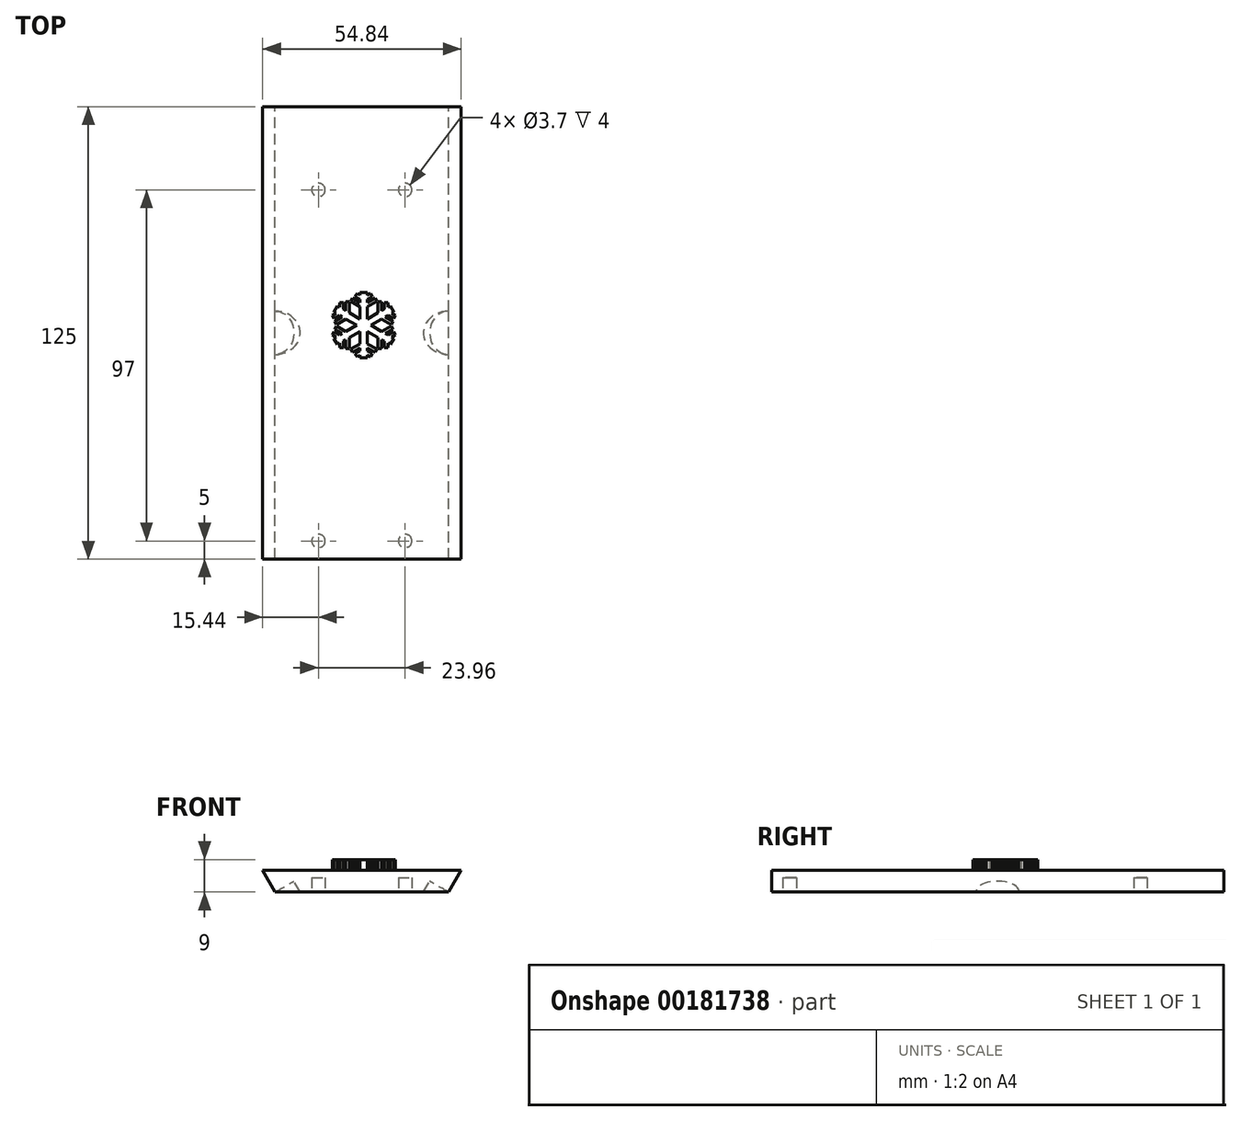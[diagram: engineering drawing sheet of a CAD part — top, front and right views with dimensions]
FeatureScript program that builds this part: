
annotation { "Feature Type Name" : "Feature", "Feature Type Description" : "" }
export const myFeature = defineFeature(function(context is Context, id is Id, definition is map)
    precondition{}
    {
        {
            var Q0;
            Q0=qCreatedBy(makeId("Front.planeOp"),FACE);
            var sketch = newSketch(context, id + "F0", { "sketchPlane" : qUnion([Q0])});
            skCircle(sketch, "E0.cCircle", {"center": v(0, 0) * mm, "radius": 47.5 * mm, "construction": true});
            skLineSegment(sketch, "E0.0", {"start": v(-27.42, -47.5) * mm, "end": v(-54.85, 0) * mm});
            skLineSegment(sketch, "E0.1", {"start": v(-54.85, 0) * mm, "end": v(-27.42, 47.5) * mm});
            skLineSegment(sketch, "E0.2", {"start": v(-27.42, 47.5) * mm, "end": v(27.42, 47.5) * mm});
            skLineSegment(sketch, "E0.3", {"start": v(27.42, 47.5) * mm, "end": v(54.85, 0) * mm});
            skLineSegment(sketch, "E0.4", {"start": v(54.85, 0) * mm, "end": v(27.42, -47.5) * mm});
            skLineSegment(sketch, "E0.5", {"start": v(27.42, -47.5) * mm, "end": v(-27.42, -47.5) * mm});
            skPoint(sketch, "E0.0.midPoint", {"position": v(-41.14, -23.75) * mm});
            skCircle(sketch, "E1.cCircle", {"center": v(0, 0) * mm, "radius": 41.5 * mm, "construction": true});
            skLineSegment(sketch, "E1.0", {"start": v(-23.96, -41.5) * mm, "end": v(-47.92, 0) * mm});
            skLineSegment(sketch, "E1.1", {"start": v(-47.92, 0) * mm, "end": v(-23.96, 41.5) * mm});
            skLineSegment(sketch, "E1.2", {"start": v(-23.96, 41.5) * mm, "end": v(23.96, 41.5) * mm});
            skLineSegment(sketch, "E1.3", {"start": v(23.96, 41.5) * mm, "end": v(47.92, 0) * mm});
            skLineSegment(sketch, "E1.4", {"start": v(47.92, 0) * mm, "end": v(23.96, -41.5) * mm});
            skLineSegment(sketch, "E1.5", {"start": v(23.96, -41.5) * mm, "end": v(-23.96, -41.5) * mm});
            skPoint(sketch, "E1.0.midPoint", {"position": v(-35.94, -20.75) * mm});
            skLineSegment(sketch, "E2", {"start": v(27.42, 47.5) * mm, "end": v(23.96, 41.5) * mm});
            skLineSegment(sketch, "E3", {"start": v(-27.42, 47.5) * mm, "end": v(-23.96, 41.5) * mm});
            skSolve(sketch);
        }
        {
            var Q0;
            Q0=makeQuery(id+"F0.imprint","IMPRINT",FACE,{"disambiguationData":[TD([[makeQuery(id+"F0.imprint","IMPRINT",EDGE,{"derivedFrom":sQuery(id+"F0.wireOp",EDGE,"E0.2")}),-1.0]])]});
            extrude(context, id + "F1", {"entities" : qUnion([Q0]), "depth" : 125 * mm});
        }
        {
            var Q0;
            Q0=makeQuery(id+"F1.opExtrude","SWEPT_FACE",FACE,{"disambiguationData":[OSD([sQuery(id+"F0.wireOp",EDGE,"E1.2")])]});
            var sketch = newSketch(context, id + "F2", { "sketchPlane" : qUnion([Q0])});
            skPoint(sketch, "E4", {"position": v(0, 125) * mm});
            skPoint(sketch, "E5", {"position": v(0, 120) * mm});
            skLineSegment(sketch, "E6", {"start": v(0, 120) * mm, "end": v(-23.96, 120) * mm});
            skPoint(sketch, "E7", {"position": v(-11.98, 120) * mm});
            skCircle(sketch, "E8", {"center": v(-11.98, 120) * mm, "radius": 1.85 * mm});
            skCircle(sketch, "E9.MirrorC", {"center": v(11.98, 120) * mm, "radius": 1.85 * mm});
            skPoint(sketch, "E10", {"position": v(0, 23) * mm});
            skLineSegment(sketch, "E11", {"start": v(0, 23) * mm, "end": v(-23.96, 23) * mm});
            skPoint(sketch, "E12", {"position": v(-11.98, 23) * mm});
            skCircle(sketch, "E13", {"center": v(-11.98, 23) * mm, "radius": 1.85 * mm});
            skCircle(sketch, "E14.MirrorC", {"center": v(11.98, 23) * mm, "radius": 1.85 * mm});
            skSolve(sketch);
        }
        {
            var Q0;
            Q0=qSketchRegion(id+"F2",true);
            extrude(context, id + "F3", {"entities" : qUnion([Q0]), "operationType" : NewBodyOperationType.REMOVE, "oppositeDirection" : true, "depth" : 4 * mm});
        }
        {
            var Q0;
            Q0=makeQuery(id+"F1.opExtrude","SWEPT_FACE",FACE,{"disambiguationData":[OSD([sQuery(id+"F0.wireOp",EDGE,"E0.2")])]});
            var sketch = newSketch(context, id + "F4", { "sketchPlane" : qUnion([Q0])});
            skPoint(sketch, "E15", {"position": v(-23.96, -62.5) * mm});
            skPoint(sketch, "E16", {"position": v(0, -90) * mm});
            skPoint(sketch, "E17", {"position": v(0, -62.5) * mm});
            skLineSegment(sketch, "E18.MirrorCS", {"start": v(-7.66, -58.59) * mm, "end": v(-8.16, -57.72) * mm});
            skLineSegment(sketch, "E19.MirrorCS", {"start": v(-7.52, -59.3) * mm, "end": v(-5.42, -58.1) * mm});
            skLineSegment(sketch, "E20.MirrorCS", {"start": v(-7.02, -60.17) * mm, "end": v(-7.52, -59.3) * mm});
            skLineSegment(sketch, "E21.MirrorCS", {"start": v(-7.02, -60.59) * mm, "end": v(-7.52, -61.45) * mm});
            skLineSegment(sketch, "E22.MirrorCS", {"start": v(6.18, -66.58) * mm, "end": v(7.18, -66.58) * mm});
            skLineSegment(sketch, "E23.MirrorCS", {"start": v(-8.16, -57.72) * mm, "end": v(-7.11, -57.12) * mm});
            skLineSegment(sketch, "E24.MirrorCS", {"start": v(6.18, -64.8) * mm, "end": v(6.18, -66.58) * mm});
            skLineSegment(sketch, "E25.MirrorCS", {"start": v(-6.11, -57.7) * mm, "end": v(-7.66, -58.59) * mm});
            skLineSegment(sketch, "E26.MirrorCS", {"start": v(4.49, -66.82) * mm, "end": v(5.49, -66.82) * mm});
            skLineSegment(sketch, "E27.MirrorCS", {"start": v(9.23, -63.04) * mm, "end": v(8.18, -63.64) * mm});
            skLineSegment(sketch, "E28.MirrorCS", {"start": v(7.18, -63.06) * mm, "end": v(8.73, -62.17) * mm});
            skLineSegment(sketch, "E29.MirrorCS", {"start": v(2.4, -69.14) * mm, "end": v(1.53, -68.64) * mm});
            skLineSegment(sketch, "E30.MirrorCS", {"start": v(8.59, -61.45) * mm, "end": v(6.49, -62.66) * mm});
            skLineSegment(sketch, "E31.MirrorCS", {"start": v(1.53, -66.68) * mm, "end": v(3.63, -67.9) * mm});
            skLineSegment(sketch, "E32.MirrorCS", {"start": v(8.73, -62.17) * mm, "end": v(9.23, -63.04) * mm});
            skLineSegment(sketch, "E33.MirrorCS", {"start": v(3.63, -67.9) * mm, "end": v(4.13, -67.03) * mm});
            skLineSegment(sketch, "E34.MirrorCS", {"start": v(-5.11, -54.18) * mm, "end": v(-6.11, -54.18) * mm});
            skLineSegment(sketch, "E35.MirrorCS", {"start": v(-1.33, -69.14) * mm, "end": v(-0.47, -68.64) * mm});
            skLineSegment(sketch, "E36.MirrorCS", {"start": v(8.09, -60.59) * mm, "end": v(8.59, -61.45) * mm});
            skLineSegment(sketch, "E37.MirrorCS", {"start": v(-4.42, -53.94) * mm, "end": v(-4.42, -56.36) * mm});
            skLineSegment(sketch, "E38.MirrorCS", {"start": v(-3.42, -53.94) * mm, "end": v(-4.42, -53.94) * mm});
            skLineSegment(sketch, "E39.MirrorCS", {"start": v(-6.11, -54.18) * mm, "end": v(-6.11, -55.39) * mm});
            skLineSegment(sketch, "E40.MirrorCS", {"start": v(2.9, -68.27) * mm, "end": v(1.53, -67.48) * mm});
            skLineSegment(sketch, "E41.MirrorCS", {"start": v(2.4, -69.14) * mm, "end": v(2.9, -68.27) * mm});
            skLineSegment(sketch, "E42.MirrorCS", {"start": v(-2.54, -52.88) * mm, "end": v(-3.06, -53.74) * mm});
            skLineSegment(sketch, "E43.MirrorCS", {"start": v(8.09, -60.17) * mm, "end": v(8.59, -59.3) * mm});
            skLineSegment(sketch, "E44.MirrorCS", {"start": v(-5.11, -55.96) * mm, "end": v(-5.11, -54.18) * mm});
            skLineSegment(sketch, "E45.MirrorCS", {"start": v(8.83, -64.01) * mm, "end": v(7.83, -65.75) * mm});
            skLineSegment(sketch, "E46.MirrorCS", {"start": v(-5.11, -66.58) * mm, "end": v(-6.11, -66.58) * mm});
            skLineSegment(sketch, "E47.MirrorCS", {"start": v(-3.42, -66.82) * mm, "end": v(-4.42, -66.82) * mm});
            skLineSegment(sketch, "E48.MirrorCS", {"start": v(5.49, -62.09) * mm, "end": v(8.09, -60.59) * mm});
            skLineSegment(sketch, "E49.MirrorCS", {"start": v(-7.76, -56.75) * mm, "end": v(-6.76, -55.01) * mm});
            skLineSegment(sketch, "E50.MirrorCS", {"start": v(-8.16, -63.04) * mm, "end": v(-7.11, -63.64) * mm});
            skLineSegment(sketch, "E51.MirrorCS", {"start": v(-3.42, -63.82) * mm, "end": v(-3.42, -66.82) * mm});
            skLineSegment(sketch, "E52.MirrorCS", {"start": v(2.4, -51.63) * mm, "end": v(1.53, -52.13) * mm});
            skLineSegment(sketch, "E53.MirrorCS", {"start": v(-6.11, -63.06) * mm, "end": v(-7.66, -62.17) * mm});
            skLineSegment(sketch, "E54.MirrorCS", {"start": v(-7.52, -61.45) * mm, "end": v(-5.42, -62.66) * mm});
            skLineSegment(sketch, "E55.MirrorCS", {"start": v(5.49, -66.82) * mm, "end": v(5.49, -64.4) * mm});
            skLineSegment(sketch, "E56.MirrorCS", {"start": v(-6.11, -66.58) * mm, "end": v(-6.11, -65.37) * mm});
            skLineSegment(sketch, "E57.MirrorCS", {"start": v(-5.11, -64.8) * mm, "end": v(-5.11, -66.58) * mm});
            skLineSegment(sketch, "E58.MirrorCS", {"start": v(-0.47, -69.38) * mm, "end": v(1.53, -69.38) * mm});
            skLineSegment(sketch, "E59.MirrorCS", {"start": v(1.53, -54.08) * mm, "end": v(3.63, -52.87) * mm});
            skLineSegment(sketch, "E60.MirrorCS", {"start": v(-4.42, -66.82) * mm, "end": v(-4.42, -64.4) * mm});
            skLineSegment(sketch, "E61.MirrorCS", {"start": v(4.49, -63.82) * mm, "end": v(4.49, -66.82) * mm});
            skLineSegment(sketch, "E62.MirrorCS", {"start": v(2.9, -52.5) * mm, "end": v(1.53, -53.28) * mm});
            skLineSegment(sketch, "E63.MirrorCS", {"start": v(2.4, -51.63) * mm, "end": v(2.9, -52.5) * mm});
            skLineSegment(sketch, "E64.MirrorCS", {"start": v(-2.54, -67.88) * mm, "end": v(-3.06, -67.03) * mm});
            skLineSegment(sketch, "E65.MirrorCS", {"start": v(-1.33, -51.63) * mm, "end": v(-0.47, -52.13) * mm});
            skLineSegment(sketch, "E66.MirrorCS", {"start": v(-3.06, -67.03) * mm, "end": v(-0.47, -65.53) * mm});
            skLineSegment(sketch, "E67.MirrorCS", {"start": v(8.73, -58.59) * mm, "end": v(9.23, -57.72) * mm});
            skLineSegment(sketch, "E68.MirrorCS", {"start": v(-0.47, -66.68) * mm, "end": v(-2.54, -67.88) * mm});
            skLineSegment(sketch, "E69.MirrorCS", {"start": v(7.18, -57.7) * mm, "end": v(8.73, -58.59) * mm});
            skLineSegment(sketch, "E70.MirrorCS", {"start": v(9.23, -57.72) * mm, "end": v(8.18, -57.12) * mm});
            skLineSegment(sketch, "E71.MirrorCS", {"start": v(-1.33, -69.14) * mm, "end": v(-1.85, -68.28) * mm});
            skLineSegment(sketch, "E72.MirrorCS", {"start": v(-1.85, -68.28) * mm, "end": v(-0.47, -67.48) * mm});
            skLineSegment(sketch, "E73.MirrorCS", {"start": v(8.59, -59.3) * mm, "end": v(6.49, -58.1) * mm});
            skLineSegment(sketch, "E74.MirrorCS", {"start": v(-6.76, -55.01) * mm, "end": v(8.83, -64.01) * mm});
            skLineSegment(sketch, "E75.MirrorCS", {"start": v(5.49, -58.67) * mm, "end": v(8.09, -60.17) * mm});
            skLineSegment(sketch, "E76.MirrorCS", {"start": v(4.13, -53.74) * mm, "end": v(1.53, -55.24) * mm});
            skLineSegment(sketch, "E77.MirrorCS", {"start": v(-0.47, -69.38) * mm, "end": v(-0.47, -51.38) * mm});
            skLineSegment(sketch, "E78.MirrorCS", {"start": v(3.63, -52.87) * mm, "end": v(4.13, -53.74) * mm});
            skLineSegment(sketch, "E79.MirrorCS", {"start": v(-0.47, -51.38) * mm, "end": v(1.53, -51.38) * mm});
            skLineSegment(sketch, "E80.MirrorCS", {"start": v(-4.42, -58.67) * mm, "end": v(-7.02, -60.17) * mm});
            skLineSegment(sketch, "E81.MirrorCS", {"start": v(4.13, -67.03) * mm, "end": v(1.53, -65.53) * mm});
            skLineSegment(sketch, "E82.MirrorCS", {"start": v(4.49, -56.94) * mm, "end": v(4.49, -53.94) * mm});
            skLineSegment(sketch, "E83.MirrorCS", {"start": v(-6.76, -65.75) * mm, "end": v(-7.76, -64.01) * mm});
            skLineSegment(sketch, "E84.MirrorCS", {"start": v(-0.47, -54.08) * mm, "end": v(-2.54, -52.88) * mm});
            skLineSegment(sketch, "E85.MirrorCS", {"start": v(-7.66, -62.17) * mm, "end": v(-8.16, -63.04) * mm});
            skLineSegment(sketch, "E86.MirrorCS", {"start": v(7.18, -66.58) * mm, "end": v(7.18, -65.37) * mm});
            skLineSegment(sketch, "E87.MirrorCS", {"start": v(4.49, -53.94) * mm, "end": v(5.49, -53.94) * mm});
            skLineSegment(sketch, "E88.MirrorCS", {"start": v(5.49, -53.94) * mm, "end": v(5.49, -56.36) * mm});
            skLineSegment(sketch, "E89.MirrorCS", {"start": v(7.18, -54.18) * mm, "end": v(7.18, -55.39) * mm});
            skLineSegment(sketch, "E90.MirrorCS", {"start": v(-4.42, -62.09) * mm, "end": v(-7.02, -60.59) * mm});
            skLineSegment(sketch, "E91.MirrorCS", {"start": v(7.83, -55.01) * mm, "end": v(8.83, -56.75) * mm});
            skLineSegment(sketch, "E92.MirrorCS", {"start": v(6.18, -55.96) * mm, "end": v(6.18, -54.18) * mm});
            skLineSegment(sketch, "E93.MirrorCS", {"start": v(-3.06, -53.74) * mm, "end": v(-0.47, -55.24) * mm});
            skLineSegment(sketch, "E94.MirrorCS", {"start": v(-3.42, -56.94) * mm, "end": v(-3.42, -53.94) * mm});
            skLineSegment(sketch, "E95.MirrorCS", {"start": v(-1.33, -51.63) * mm, "end": v(-1.85, -52.48) * mm});
            skLineSegment(sketch, "E96.MirrorCS", {"start": v(8.83, -56.75) * mm, "end": v(-6.76, -65.75) * mm});
            skLineSegment(sketch, "E97.MirrorCS", {"start": v(6.18, -54.18) * mm, "end": v(7.18, -54.18) * mm});
            skLineSegment(sketch, "E98.MirrorCS", {"start": v(-1.85, -52.48) * mm, "end": v(-0.47, -53.28) * mm});
            skLineSegment(sketch, "E99.MirrorCS", {"start": v(1.53, -69.38) * mm, "end": v(1.53, -51.38) * mm});
            skPoint(sketch, "E100.MirrorP", {"position": v(0.53, -61.54) * mm});
            skPoint(sketch, "E101.MirrorP", {"position": v(0.53, -60.38) * mm});
            skLineSegment(sketch, "E102.MirrorCS", {"start": v(-7.76, -64.01) * mm, "end": v(7.83, -55.01) * mm});
            skPoint(sketch, "E103.MirrorP", {"position": v(1.53, -60.96) * mm});
            skLineSegment(sketch, "E104.MirrorCS", {"start": v(7.83, -65.75) * mm, "end": v(-7.76, -56.75) * mm});
            skPoint(sketch, "E105.MirrorP", {"position": v(0.53, -59.23) * mm});
            skPoint(sketch, "E106.MirrorP", {"position": v(-1.47, -60.38) * mm});
            skPoint(sketch, "E107.MirrorP", {"position": v(-0.47, -58.65) * mm});
            skPoint(sketch, "E108.MirrorP", {"position": v(1.53, -59.8) * mm});
            skLineSegment(sketch, "E109.MirrorCS", {"start": v(10.53, -70.38) * mm, "end": v(10.53, -50.38) * mm});
            skPoint(sketch, "E110.MirrorP", {"position": v(2.53, -60.38) * mm});
            skPoint(sketch, "E111.MirrorP", {"position": v(1.53, -58.65) * mm});
            skPoint(sketch, "E112.MirrorP", {"position": v(-0.47, -62.11) * mm});
            skPoint(sketch, "E113.MirrorP", {"position": v(-0.47, -59.8) * mm});
            skPoint(sketch, "E114.MirrorP", {"position": v(-0.47, -60.96) * mm});
            skPoint(sketch, "E115.MirrorP", {"position": v(0.32, -60.05) * mm});
            skPoint(sketch, "E116.MirrorP", {"position": v(1.53, -62.11) * mm});
            skLineSegment(sketch, "E117.MirrorCS", {"start": v(-9.47, -70.38) * mm, "end": v(-9.47, -50.38) * mm});
            skCircle(sketch, "E118.MirrorC", {"center": v(0.53, -60.38) * mm, "radius": 10.52 * mm});
            skCircle(sketch, "E119.MirrorC", {"center": v(0.53, -60.38) * mm, "radius": 11.52 * mm});
            skPoint(sketch, "E120.MirrorP", {"position": v(8.33, -55.88) * mm});
            skPoint(sketch, "E121.MirrorP", {"position": v(-7.26, -55.88) * mm});
            skLineSegment(sketch, "E122.MirrorCS", {"start": v(-9.47, -70.38) * mm, "end": v(10.53, -70.38) * mm});
            skLineSegment(sketch, "E123.MirrorCS", {"start": v(-9.47, -50.38) * mm, "end": v(10.53, -50.38) * mm});
            skPoint(sketch, "E124.MirrorP", {"position": v(8.33, -64.88) * mm});
            skPoint(sketch, "E125.MirrorP", {"position": v(-3.36, -53.63) * mm});
            skPoint(sketch, "E126.MirrorP", {"position": v(0.53, -51.38) * mm});
            skPoint(sketch, "E127.MirrorP", {"position": v(0.53, -50.38) * mm});
            skPoint(sketch, "E128.MirrorP", {"position": v(-9.47, -60.38) * mm});
            skPoint(sketch, "E129.MirrorP", {"position": v(-7.26, -64.88) * mm});
            skPoint(sketch, "E130.MirrorP", {"position": v(0.53, -69.38) * mm});
            skSolve(sketch);
        }
        {
            var Q0;
            {var subQ7=sQuery(id+"F4.wireOp",EDGE,"E58.MirrorCS");Q0=makeQuery(id+"F4.imprint","IMPRINT",FACE,{"disambiguationData":[TD([[makeQuery(id+"F4.imprint","IMPRINT",EDGE,{"derivedFrom":subQ7}),1.0]])]});}
            var Q1;
            {var subQ0=sQuery(id+"F4.wireOp",EDGE,"E29.MirrorCS");Q1=makeQuery(id+"F4.imprint","IMPRINT",FACE,{"disambiguationData":[TD([[makeQuery(id+"F4.imprint","IMPRINT",EDGE,{"derivedFrom":subQ0}),-1.0]])]});}
            var Q2;
            {var subQ0=sQuery(id+"F4.wireOp",EDGE,"E31.MirrorCS");Q2=makeQuery(id+"F4.imprint","IMPRINT",FACE,{"disambiguationData":[TD([[makeQuery(id+"F4.imprint","IMPRINT",EDGE,{"derivedFrom":subQ0}),1.0]])]});}
            var Q3;
            {var subQ0=sQuery(id+"F4.wireOp",EDGE,"E35.MirrorCS");Q3=makeQuery(id+"F4.imprint","IMPRINT",FACE,{"disambiguationData":[TD([[makeQuery(id+"F4.imprint","IMPRINT",EDGE,{"derivedFrom":subQ0}),1.0]])]});}
            var Q4;
            Q4=makeQuery(id+"F4.imprint","IMPRINT",FACE,{"disambiguationData":[TD([[makeQuery(id+"F4.imprint","IMPRINT",EDGE,{"derivedFrom":sQuery(id+"F4.wireOp",EDGE,"E64.MirrorCS")}),-1.0]])]});
            var Q5;
            Q5=makeQuery(id+"F4.imprint","IMPRINT",FACE,{"disambiguationData":[TD([[makeQuery(id+"F4.imprint","IMPRINT",EDGE,{"derivedFrom":sQuery(id+"F4.wireOp",EDGE,"E47.MirrorCS")}),-1.0]])]});
            var Q6;
            Q6=makeQuery(id+"F4.imprint","IMPRINT",FACE,{"disambiguationData":[TD([[makeQuery(id+"F4.imprint","IMPRINT",EDGE,{"derivedFrom":sQuery(id+"F4.wireOp",EDGE,"E46.MirrorCS")}),-1.0]])]});
            var Q7;
            {var subQ0=sQuery(id+"F4.wireOp",EDGE,"E50.MirrorCS");Q7=makeQuery(id+"F4.imprint","IMPRINT",FACE,{"disambiguationData":[TD([[makeQuery(id+"F4.imprint","IMPRINT",EDGE,{"derivedFrom":subQ0}),1.0]])]});}
            var Q8;
            Q8=makeQuery(id+"F4.imprint","IMPRINT",FACE,{"disambiguationData":[TD([[makeQuery(id+"F4.imprint","IMPRINT",EDGE,{"derivedFrom":sQuery(id+"F4.wireOp",EDGE,"E21.MirrorCS")}),1.0]])]});
            var Q9;
            {var subQ0=sQuery(id+"F4.wireOp",EDGE,"E19.MirrorCS");Q9=makeQuery(id+"F4.imprint","IMPRINT",FACE,{"disambiguationData":[TD([[makeQuery(id+"F4.imprint","IMPRINT",EDGE,{"derivedFrom":subQ0}),-1.0]])]});}
            var Q10;
            Q10=makeQuery(id+"F4.imprint","IMPRINT",FACE,{"disambiguationData":[TD([[makeQuery(id+"F4.imprint","IMPRINT",EDGE,{"derivedFrom":sQuery(id+"F4.wireOp",EDGE,"E18.MirrorCS")}),-1.0]])]});
            var Q11;
            Q11=makeQuery(id+"F4.imprint","IMPRINT",FACE,{"disambiguationData":[TD([[makeQuery(id+"F4.imprint","IMPRINT",EDGE,{"derivedFrom":sQuery(id+"F4.wireOp",EDGE,"E34.MirrorCS")}),1.0]])]});
            var Q12;
            {var subQ0=sQuery(id+"F4.wireOp",EDGE,"E37.MirrorCS");Q12=makeQuery(id+"F4.imprint","IMPRINT",FACE,{"disambiguationData":[TD([[makeQuery(id+"F4.imprint","IMPRINT",EDGE,{"derivedFrom":subQ0}),1.0]])]});}
            var Q13;
            Q13=makeQuery(id+"F4.imprint","IMPRINT",FACE,{"disambiguationData":[TD([[makeQuery(id+"F4.imprint","IMPRINT",EDGE,{"derivedFrom":sQuery(id+"F4.wireOp",EDGE,"E42.MirrorCS")}),1.0]])]});
            var Q14;
            {var subQ0=sQuery(id+"F4.wireOp",EDGE,"E65.MirrorCS");Q14=makeQuery(id+"F4.imprint","IMPRINT",FACE,{"disambiguationData":[TD([[makeQuery(id+"F4.imprint","IMPRINT",EDGE,{"derivedFrom":subQ0}),-1.0]])]});}
            var Q15;
            {var subQ0=sQuery(id+"F4.wireOp",EDGE,"E52.MirrorCS");Q15=makeQuery(id+"F4.imprint","IMPRINT",FACE,{"disambiguationData":[TD([[makeQuery(id+"F4.imprint","IMPRINT",EDGE,{"derivedFrom":subQ0}),1.0]])]});}
            var Q16;
            {var subQ0=sQuery(id+"F4.wireOp",EDGE,"E59.MirrorCS");Q16=makeQuery(id+"F4.imprint","IMPRINT",FACE,{"disambiguationData":[TD([[makeQuery(id+"F4.imprint","IMPRINT",EDGE,{"derivedFrom":subQ0}),-1.0]])]});}
            var Q17;
            {var subQ0=sQuery(id+"F4.wireOp",EDGE,"E82.MirrorCS");Q17=makeQuery(id+"F4.imprint","IMPRINT",FACE,{"disambiguationData":[TD([[makeQuery(id+"F4.imprint","IMPRINT",EDGE,{"derivedFrom":subQ0}),-1.0]])]});}
            var Q18;
            {var subQ0=sQuery(id+"F4.wireOp",EDGE,"E89.MirrorCS");Q18=makeQuery(id+"F4.imprint","IMPRINT",FACE,{"disambiguationData":[TD([[makeQuery(id+"F4.imprint","IMPRINT",EDGE,{"derivedFrom":subQ0}),-1.0]])]});}
            var Q19;
            Q19=makeQuery(id+"F4.imprint","IMPRINT",FACE,{"disambiguationData":[TD([[makeQuery(id+"F4.imprint","IMPRINT",EDGE,{"derivedFrom":sQuery(id+"F4.wireOp",EDGE,"E67.MirrorCS")}),1.0]])]});
            var Q20;
            Q20=makeQuery(id+"F4.imprint","IMPRINT",FACE,{"disambiguationData":[TD([[makeQuery(id+"F4.imprint","IMPRINT",EDGE,{"derivedFrom":sQuery(id+"F4.wireOp",EDGE,"E43.MirrorCS")}),1.0]])]});
            var Q21;
            {var subQ0=sQuery(id+"F4.wireOp",EDGE,"E30.MirrorCS");Q21=makeQuery(id+"F4.imprint","IMPRINT",FACE,{"disambiguationData":[TD([[makeQuery(id+"F4.imprint","IMPRINT",EDGE,{"derivedFrom":subQ0}),-1.0]])]});}
            var Q22;
            {var subQ0=sQuery(id+"F4.wireOp",EDGE,"E27.MirrorCS");Q22=makeQuery(id+"F4.imprint","IMPRINT",FACE,{"disambiguationData":[TD([[makeQuery(id+"F4.imprint","IMPRINT",EDGE,{"derivedFrom":subQ0}),-1.0]])]});}
            var Q23;
            Q23=makeQuery(id+"F4.imprint","IMPRINT",FACE,{"disambiguationData":[TD([[makeQuery(id+"F4.imprint","IMPRINT",EDGE,{"derivedFrom":sQuery(id+"F4.wireOp",EDGE,"E22.MirrorCS")}),1.0]])]});
            var Q24;
            {var subQ3=sQuery(id+"F4.wireOp",EDGE,"E45.MirrorCS");Q24=makeQuery(id+"F4.imprint","IMPRINT",FACE,{"disambiguationData":[TD([[makeQuery(id+"F4.imprint","IMPRINT",EDGE,{"derivedFrom":subQ3}),-1.0]])]});}
            var Q25;
            {var subQ5=sQuery(id+"F4.wireOp",EDGE,"E83.MirrorCS");Q25=makeQuery(id+"F4.imprint","IMPRINT",FACE,{"disambiguationData":[TD([[makeQuery(id+"F4.imprint","IMPRINT",EDGE,{"derivedFrom":subQ5}),-1.0]])]});}
            var Q26;
            {var subQ9=sQuery(id+"F4.wireOp",EDGE,"E49.MirrorCS");Q26=makeQuery(id+"F4.imprint","IMPRINT",FACE,{"disambiguationData":[TD([[makeQuery(id+"F4.imprint","IMPRINT",EDGE,{"derivedFrom":subQ9}),-1.0]])]});}
            var Q27;
            {var subQ15=sQuery(id+"F4.wireOp",EDGE,"E91.MirrorCS");Q27=makeQuery(id+"F4.imprint","IMPRINT",FACE,{"disambiguationData":[TD([[makeQuery(id+"F4.imprint","IMPRINT",EDGE,{"derivedFrom":subQ15}),-1.0]])]});}
            var Q28;
            {var subQ10=sQuery(id+"F4.wireOp",EDGE,"E79.MirrorCS");Q28=makeQuery(id+"F4.imprint","IMPRINT",FACE,{"disambiguationData":[TD([[makeQuery(id+"F4.imprint","IMPRINT",EDGE,{"derivedFrom":subQ10}),-1.0]])]});}
            var Q29;
            Q29=makeQuery(id+"F4.imprint","IMPRINT",FACE,{"disambiguationData":[TD([[makeQuery(id+"F4.imprint","IMPRINT",EDGE,{"derivedFrom":sQuery(id+"F4.wireOp",EDGE,"E26.MirrorCS")}),1.0]])]});
            var Q30;
            {var subQ0=sQuery(id+"F4.wireOp",EDGE,"E96.MirrorCS");var subQ1=sQuery(id+"F4.wireOp",EDGE,"E77.MirrorCS");var subQ2=makeQuery(id+"F4.imprint","INTERSECT",VERTEX,{"derivedFrom":[subQ1,subQ0]});Q30=makeQuery(id+"F4.imprint","IMPRINT",FACE,{"disambiguationData":[TD([[makeQuery(id+"F4.imprint","IMPRINT",EDGE,{"disambiguationData":[TD([[subQ2,-1.0]])],"derivedFrom":subQ1}),-1.0]])]});}
            var Q31;
            {var subQ0=sQuery(id+"F4.wireOp",EDGE,"E99.MirrorCS");var subQ1=sQuery(id+"F4.wireOp",EDGE,"E96.MirrorCS");var subQ2=makeQuery(id+"F4.imprint","INTERSECT",VERTEX,{"derivedFrom":[subQ1,subQ0]});Q31=makeQuery(id+"F4.imprint","IMPRINT",FACE,{"disambiguationData":[TD([[makeQuery(id+"F4.imprint","IMPRINT",EDGE,{"disambiguationData":[TD([[subQ2,-1.0]])],"derivedFrom":subQ1}),1.0]])]});}
            var Q32;
            {var subQ0=sQuery(id+"F4.wireOp",EDGE,"E99.MirrorCS");var subQ1=sQuery(id+"F4.wireOp",EDGE,"E74.MirrorCS");var subQ2=makeQuery(id+"F4.imprint","INTERSECT",VERTEX,{"derivedFrom":[subQ1,subQ0]});Q32=makeQuery(id+"F4.imprint","IMPRINT",FACE,{"disambiguationData":[TD([[makeQuery(id+"F4.imprint","IMPRINT",EDGE,{"disambiguationData":[TD([[subQ2,-1.0]])],"derivedFrom":subQ1}),-1.0]])]});}
            var Q33;
            {var subQ0=sQuery(id+"F4.wireOp",EDGE,"E102.MirrorCS");var subQ1=sQuery(id+"F4.wireOp",EDGE,"E74.MirrorCS");var subQ2=makeQuery(id+"F4.imprint","INTERSECT",VERTEX,{"derivedFrom":[subQ1,subQ0]});Q33=makeQuery(id+"F4.imprint","IMPRINT",FACE,{"disambiguationData":[TD([[makeQuery(id+"F4.imprint","IMPRINT",EDGE,{"disambiguationData":[TD([[subQ2,-1.0]])],"derivedFrom":subQ1}),1.0]])]});}
            var Q34;
            {var subQ5=sQuery(id+"F4.wireOp",EDGE,"E74.MirrorCS");var subQ9=sQuery(id+"F4.wireOp",EDGE,"E102.MirrorCS");var subQ11=makeQuery(id+"F4.imprint","INTERSECT",VERTEX,{"derivedFrom":[subQ5,subQ9]});Q34=makeQuery(id+"F4.imprint","IMPRINT",FACE,{"disambiguationData":[TD([[makeQuery(id+"F4.imprint","IMPRINT",EDGE,{"disambiguationData":[TD([[subQ11,-1.0]])],"derivedFrom":subQ5}),-1.0]])]});}
            var Q35;
            {var subQ0=sQuery(id+"F4.wireOp",EDGE,"E104.MirrorCS");var subQ1=sQuery(id+"F4.wireOp",EDGE,"E77.MirrorCS");var subQ2=makeQuery(id+"F4.imprint","INTERSECT",VERTEX,{"derivedFrom":[subQ1,subQ0]});Q35=makeQuery(id+"F4.imprint","IMPRINT",FACE,{"disambiguationData":[TD([[makeQuery(id+"F4.imprint","IMPRINT",EDGE,{"disambiguationData":[TD([[subQ2,-1.0]])],"derivedFrom":subQ1}),1.0]])]});}
            var Q36;
            {var subQ0=sQuery(id+"F4.wireOp",EDGE,"E77.MirrorCS");var subQ1=sQuery(id+"F4.wireOp",EDGE,"E74.MirrorCS");var subQ2=makeQuery(id+"F4.imprint","INTERSECT",VERTEX,{"derivedFrom":[subQ1,subQ0]});Q36=makeQuery(id+"F4.imprint","IMPRINT",FACE,{"disambiguationData":[TD([[makeQuery(id+"F4.imprint","IMPRINT",EDGE,{"disambiguationData":[TD([[subQ2,-1.0]])],"derivedFrom":subQ1}),-1.0]])]});}
            extrude(context, id + "F5", {"entities" : qUnion([Q0, Q1, Q2, Q3, Q4, Q5, Q6, Q7, Q8, Q9, Q10, Q11, Q12, Q13, Q14, Q15, Q16, Q17, Q18, Q19, Q20, Q21, Q22, Q23, Q24, Q25, Q26, Q27, Q28, Q29, Q30, Q31, Q32, Q33, Q34, Q35, Q36]), "operationType" : NewBodyOperationType.ADD, "depth" : 3 * mm});
        }
        {
            var Q0;
            Q0=makeQuery(id+"F1.opExtrude","SWEPT_EDGE",EDGE,{"disambiguationData":[OSD([sQuery(id+"F0.wireOp",EDGE,"E1.1"),sQuery(id+"F0.wireOp",EDGE,"E1.2"),sQuery(id+"F0.wireOp",EDGE,"E3")])]});
            cPlane(context, id + "F6", {"entities" : qUnion([Q0]), "cplaneType" : CPlaneType.LINE_ANGLE, "offset" : 25 * mm, "angle" : 150 * degree, "width" : 150 * mm, "height" : 150 * mm});
        }
        {
            var Q0;
            Q0=qCreatedBy(id+"F6.planeOp",FACE);
            var sketch = newSketch(context, id + "F7", { "sketchPlane" : qUnion([Q0])});
            skCircle(sketch, "E131", {"center": v(0, 62.5) * mm, "radius": 6 * mm});
            skSolve(sketch);
        }
        {
            var Q0;
            Q0=qSketchRegion(id+"F7",true);
            extrude(context, id + "F8", {"entities" : qUnion([Q0]), "operationType" : NewBodyOperationType.REMOVE, "depth" : 25 * mm});
        }
        {
            var Q0;
            Q0=makeQuery(id+"F1.opExtrude","SWEPT_EDGE",EDGE,{"disambiguationData":[OSD([sQuery(id+"F0.wireOp",EDGE,"E1.2"),sQuery(id+"F0.wireOp",EDGE,"E1.3"),sQuery(id+"F0.wireOp",EDGE,"E2")])]});
            cPlane(context, id + "F9", {"entities" : qUnion([Q0]), "cplaneType" : CPlaneType.LINE_ANGLE, "offset" : 25 * mm, "angle" : 30 * degree, "width" : 150 * mm, "height" : 150 * mm});
        }
        {
            var Q0;
            Q0=qCreatedBy(id+"F9.planeOp",FACE);
            var sketch = newSketch(context, id + "F10", { "sketchPlane" : qUnion([Q0])});
            skCircle(sketch, "E132", {"center": v(0, -62.5) * mm, "radius": 6 * mm});
            skSolve(sketch);
        }
        {
            var Q0;
            Q0=qSketchRegion(id+"F10",true);
            extrude(context, id + "F11", {"entities" : qUnion([Q0]), "operationType" : NewBodyOperationType.REMOVE, "oppositeDirection" : true, "depth" : 25 * mm});
        }
    });
